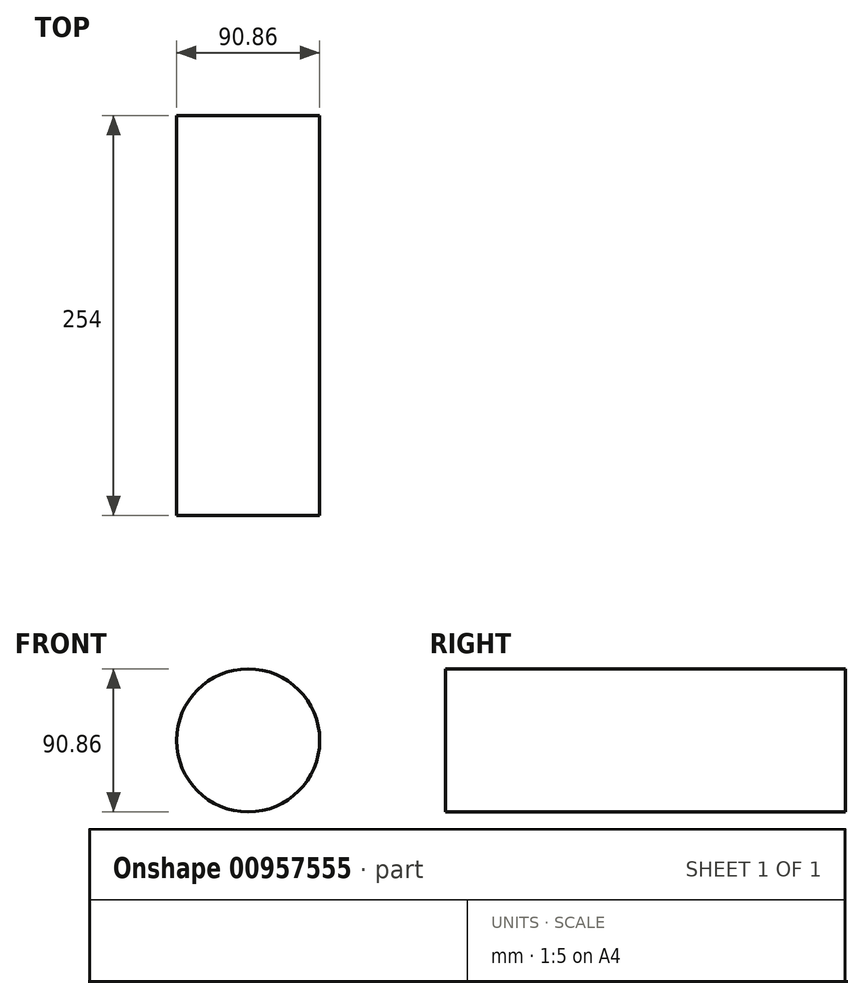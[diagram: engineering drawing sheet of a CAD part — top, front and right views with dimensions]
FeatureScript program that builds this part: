
annotation { "Feature Type Name" : "Feature", "Feature Type Description" : "" }
export const myFeature = defineFeature(function(context is Context, id is Id, definition is map)
    precondition{}
    {
        {
            var Q0;
            Q0=qCreatedBy(makeId("Front.planeOp"),FACE);
            var sketch = newSketch(context, id + "F0", { "sketchPlane" : qUnion([Q0])});
            skCircle(sketch, "E0", {"center": v(0, 0) * mm, "radius": 45.43 * mm});
            skSolve(sketch);
        }
        {
            var Q0;
            Q0=sQuery(id+"F0.wireOp",EDGE,"E0");
            extrude(context, id + "F1", {"bodyType" : ToolBodyType.SURFACE, "surfaceEntities" : qUnion([Q0]), "depth" : 254 * mm, "offsetDistance" : 25.4 * mm});
        }
    });
